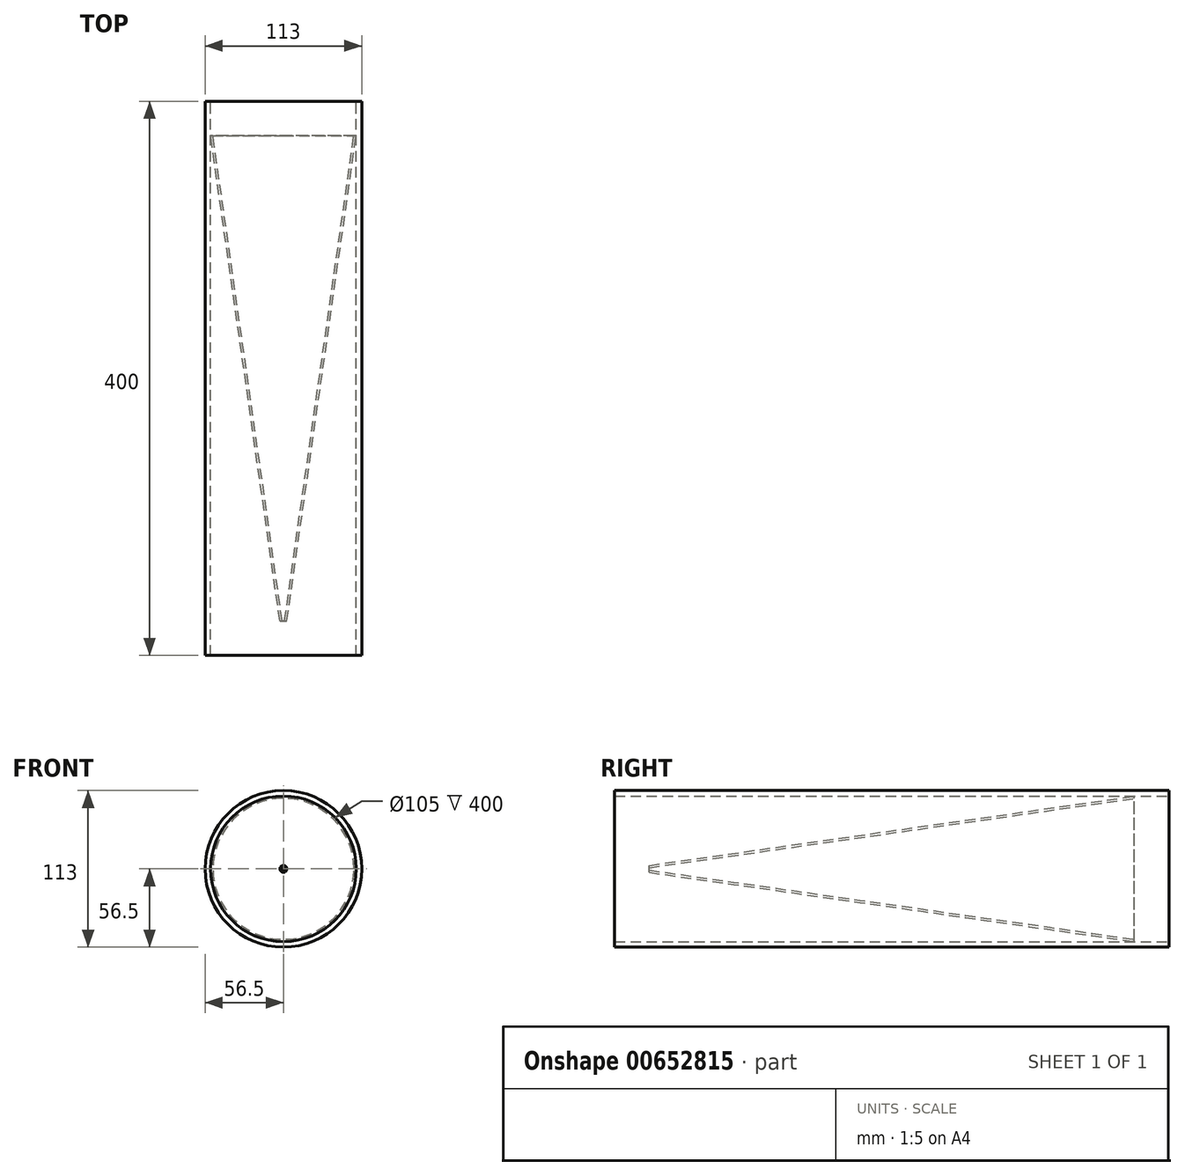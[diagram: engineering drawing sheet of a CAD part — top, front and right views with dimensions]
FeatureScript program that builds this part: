
annotation { "Feature Type Name" : "Feature", "Feature Type Description" : "" }
export const myFeature = defineFeature(function(context is Context, id is Id, definition is map)
    precondition{}
    {
        {
            var Q0;
            Q0=qCreatedBy(makeId("Front.planeOp"),FACE);
            var sketch = newSketch(context, id + "F0", { "sketchPlane" : qUnion([Q0])});
            skCircle(sketch, "E0", {"center": v(0, 0) * mm, "radius": 52.5 * mm});
            skCircle(sketch, "E1", {"center": v(0, 0) * mm, "radius": 56.5 * mm});
            skSolve(sketch);
        }
        {
            var Q0;
            Q0=qCreatedBy(makeId("Front.planeOp"),FACE);
            cPlane(context, id + "F1", {"entities" : qUnion([Q0]), "cplaneType" : CPlaneType.OFFSET, "offset" : 350 * mm, "width" : 150 * mm, "height" : 150 * mm});
        }
        {
            var Q0;
            Q0=qCreatedBy(id+"F1.planeOp",FACE);
            var sketch = newSketch(context, id + "F2", { "sketchPlane" : qUnion([Q0])});
            skCircle(sketch, "E2", {"center": v(0, 0) * mm, "radius": 2.5 * mm});
            skSolve(sketch);
        }
        {
            var Q0;
            Q0=makeQuery(id+"F0.imprint","IMPRINT",FACE,{"disambiguationData":[TD([[makeQuery(id+"F0.imprint","IMPRINT",EDGE,{"derivedFrom":sQuery(id+"F0.wireOp",EDGE,"E0")}),1.0]])]});
            var Q1;
            Q1=makeQuery(id+"F2.imprint","IMPRINT",FACE,{"disambiguationData":[TD([[makeQuery(id+"F2.imprint","IMPRINT",EDGE,{"derivedFrom":sQuery(id+"F2.wireOp",EDGE,"E2")}),1.0]])]});
            loft(context, id + "F3", {"sheetProfilesArray" : [{ "sheetProfileEntities" : qUnion([Q0]) }, { "sheetProfileEntities" : qUnion([Q1]) }]});
        }
        {
            var Q0;
            Q0=makeQuery(id+"F3.opLoft","CAP_FACE",FACE,{"disambiguationData":[OSD([makeQuery(id+"F0.imprint","IMPRINT",FACE,{"disambiguationData":[TD([[makeQuery(id+"F0.imprint","IMPRINT",EDGE,{"derivedFrom":sQuery(id+"F0.wireOp",EDGE,"E0")}),1.0]])]})])],"isStart":true});
            var Q1;
            Q1=makeQuery(id+"F3.opLoft","CAP_FACE",FACE,{"disambiguationData":[OSD([makeQuery(id+"F2.imprint","IMPRINT",FACE,{"disambiguationData":[TD([[makeQuery(id+"F2.imprint","IMPRINT",EDGE,{"derivedFrom":sQuery(id+"F2.wireOp",EDGE,"E2")}),1.0]])]})])],"isStart":true});
            shell(context, id + "F4", {"entities" : qUnion([Q0, Q1]), "thickness" : 1.6 * mm});
        }
        {
            var Q0;
            Q0=makeQuery(id+"F0.imprint","IMPRINT",FACE,{"disambiguationData":[TD([[makeQuery(id+"F0.imprint","IMPRINT",EDGE,{"derivedFrom":sQuery(id+"F0.wireOp",EDGE,"E0")}),-1.0]])]});
            extrude(context, id + "F5", {"entities" : qUnion([Q0]), "depth" : 375 * mm, "offsetDistance" : 25 * mm, "hasSecondDirection" : true, "secondDirectionOppositeDirection" : true, "secondDirectionDepth" : 25 * mm});
        }
    });
